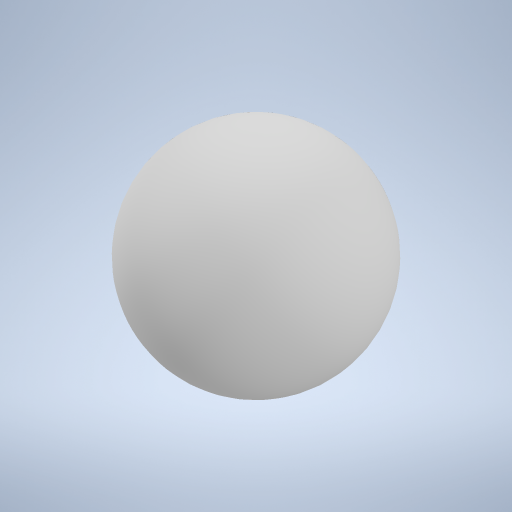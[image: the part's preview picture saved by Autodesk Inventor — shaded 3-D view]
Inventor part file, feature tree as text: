
AUTODESK INVENTOR PART (.ipt)
format: ipt  version: 2024.3 (Build 283343000, 343)  size: 231,424 bytes
history: native  units: in
note: dims shown in document units (in); Inventor stores cm internally (conversion verified against a paired STEP export)
features: revolve x1, sketch x1
ambient origin geometry x8: Origin, YZ Plane, XZ Plane, XY Plane, X Axis, Y Axis, Z Axis, Center Point
bodies: Solid1 (feature_tree)
feature tree (2):
  revolve  "Revolution1"  Angle=180.0deg
  sketch  "Sketch1"  dims[d0=0.5in d1=180.0deg]
